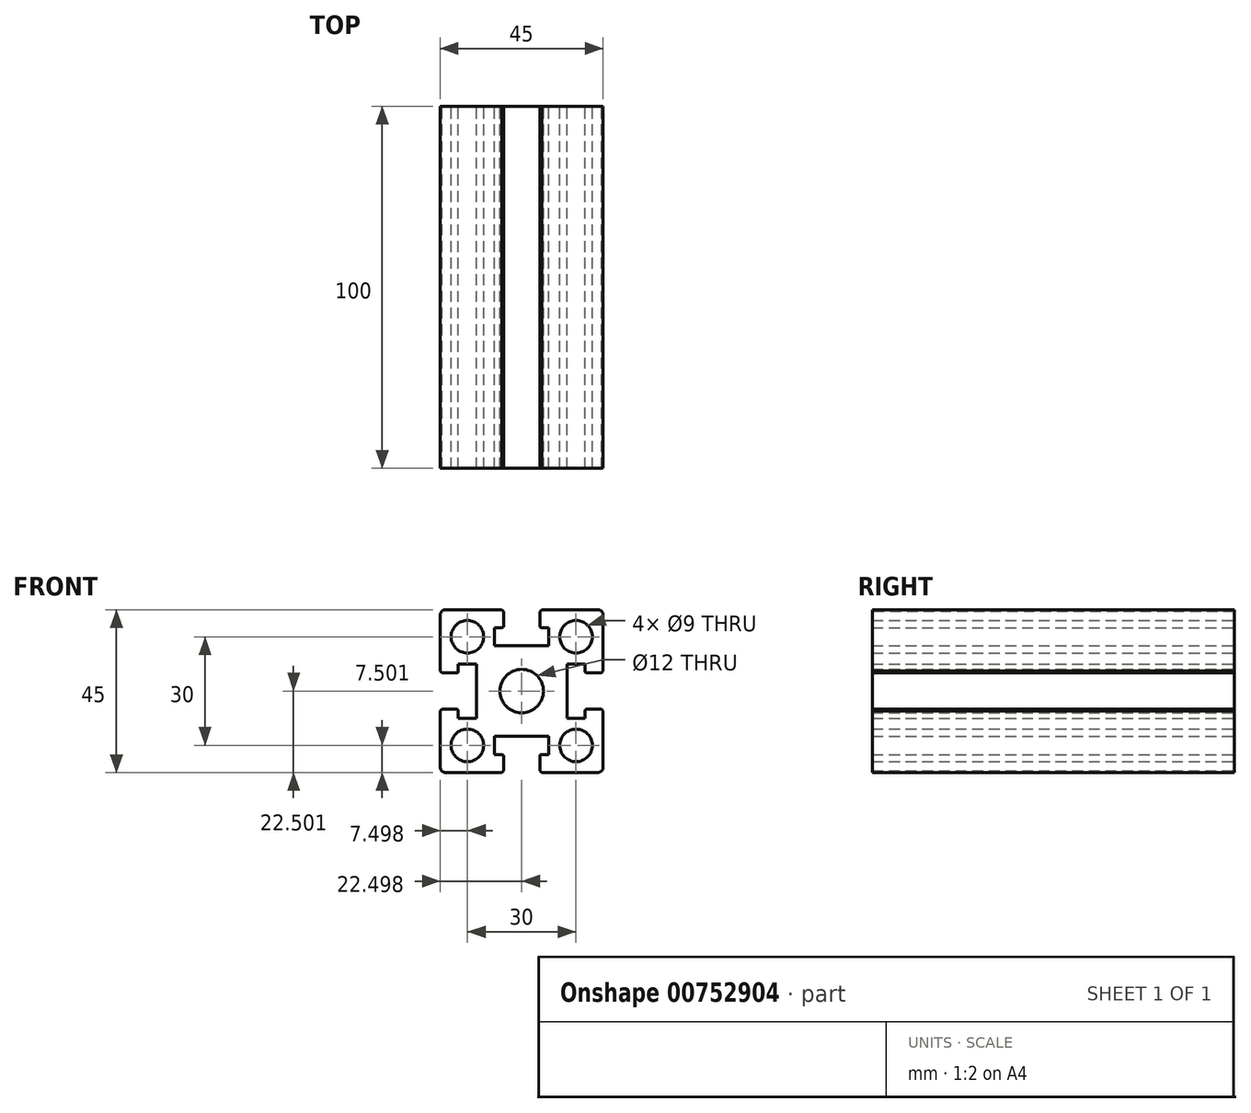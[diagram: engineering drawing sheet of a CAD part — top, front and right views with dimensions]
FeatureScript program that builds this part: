
annotation { "Feature Type Name" : "Feature", "Feature Type Description" : "" }
export const myFeature = defineFeature(function(context is Context, id is Id, definition is map)
    precondition{}
    {
        {
            var Q0;
            Q0=qCreatedBy(makeId("Front.planeOp"),FACE);
            var sketch = newSketch(context, id + "F0", { "sketchPlane" : qUnion([Q0])});
            skLineSegment(sketch, "E0.left", {"start": v(21.62, -21.03) * mm, "end": v(21.62, -3.53) * mm});
            skLineSegment(sketch, "E0.right", {"start": v(-23.38, -21.03) * mm, "end": v(-23.38, -3.53) * mm});
            skPoint(sketch, "E0.middle", {"position": v(-0.88, 1.47) * mm});
            skCircle(sketch, "E1", {"center": v(-0.88, 1.47) * mm, "radius": 6 * mm});
            skLineSegment(sketch, "E2.bottom", {"start": v(-23.38, 6.47) * mm, "end": v(-18.38, 6.47) * mm});
            skLineSegment(sketch, "E2.top", {"start": v(-23.38, -3.53) * mm, "end": v(-18.38, -3.53) * mm});
            skLineSegment(sketch, "E3", {"start": v(-18.38, 6.47) * mm, "end": v(-18.38, 8.97) * mm});
            skLineSegment(sketch, "E4", {"start": v(-18.38, 8.97) * mm, "end": v(-13.38, 8.97) * mm});
            skLineSegment(sketch, "E5", {"start": v(-13.38, 8.97) * mm, "end": v(-13.38, -6.03) * mm});
            skLineSegment(sketch, "E6", {"start": v(-18.38, -3.53) * mm, "end": v(-18.38, -6.03) * mm});
            skLineSegment(sketch, "E7", {"start": v(-18.38, -6.03) * mm, "end": v(-13.38, -6.03) * mm});
            skLineSegment(sketch, "E8.trimOffspring", {"start": v(-23.38, 6.47) * mm, "end": v(-23.38, 23.97) * mm});
            skLineSegment(sketch, "E9.MirrorCS", {"start": v(21.62, -3.53) * mm, "end": v(16.62, -3.53) * mm});
            skLineSegment(sketch, "E10.MirrorCS", {"start": v(16.62, -6.03) * mm, "end": v(11.62, -6.03) * mm});
            skLineSegment(sketch, "E11.MirrorCS", {"start": v(11.62, 8.97) * mm, "end": v(11.62, -6.03) * mm});
            skLineSegment(sketch, "E12.MirrorCS", {"start": v(16.62, 8.97) * mm, "end": v(11.62, 8.97) * mm});
            skLineSegment(sketch, "E13.MirrorCS", {"start": v(21.62, 6.47) * mm, "end": v(16.62, 6.47) * mm});
            skLineSegment(sketch, "E14", {"start": v(16.62, 8.97) * mm, "end": v(16.62, 6.47) * mm});
            skLineSegment(sketch, "E15", {"start": v(16.62, -3.53) * mm, "end": v(16.62, -6.03) * mm});
            skLineSegment(sketch, "E16.trimOffspring", {"start": v(21.62, 6.47) * mm, "end": v(21.62, 23.97) * mm});
            skPoint(sketch, "E17", {"position": v(14.12, -13.53) * mm});
            skPoint(sketch, "E18", {"position": v(14.12, 16.47) * mm});
            skPoint(sketch, "E19", {"position": v(-15.88, 16.47) * mm});
            skPoint(sketch, "E20", {"position": v(-15.88, -13.53) * mm});
            skCircle(sketch, "E21", {"center": v(14.12, -13.53) * mm, "radius": 4.5 * mm});
            skCircle(sketch, "E22", {"center": v(-15.88, -13.53) * mm, "radius": 4.5 * mm});
            skCircle(sketch, "E23", {"center": v(-15.88, 16.47) * mm, "radius": 4.5 * mm});
            skCircle(sketch, "E24", {"center": v(14.12, 16.47) * mm, "radius": 4.5 * mm});
            skLineSegment(sketch, "E25", {"start": v(-23.38, 23.97) * mm, "end": v(-5.88, 23.97) * mm});
            skLineSegment(sketch, "E26", {"start": v(-23.38, -21.03) * mm, "end": v(-5.88, -21.03) * mm});
            skLineSegment(sketch, "E27.left", {"start": v(-5.88, 23.97) * mm, "end": v(-5.88, 18.97) * mm});
            skLineSegment(sketch, "E27.right", {"start": v(4.12, 23.97) * mm, "end": v(4.12, 18.97) * mm});
            skLineSegment(sketch, "E28.bottom", {"start": v(-8.38, 18.97) * mm, "end": v(-5.88, 18.97) * mm});
            skLineSegment(sketch, "E28.top", {"start": v(-8.38, 13.97) * mm, "end": v(6.62, 13.97) * mm});
            skLineSegment(sketch, "E28.left", {"start": v(-8.38, 18.97) * mm, "end": v(-8.38, 13.97) * mm});
            skLineSegment(sketch, "E28.right", {"start": v(6.62, 18.97) * mm, "end": v(6.62, 13.97) * mm});
            skLineSegment(sketch, "E29.trimOffspring", {"start": v(4.12, 23.97) * mm, "end": v(21.62, 23.97) * mm});
            skLineSegment(sketch, "E30.trimOffspring", {"start": v(4.12, 18.97) * mm, "end": v(6.62, 18.97) * mm});
            skLineSegment(sketch, "E31.left", {"start": v(-5.88, -21.03) * mm, "end": v(-5.88, -16.03) * mm});
            skLineSegment(sketch, "E31.right", {"start": v(4.12, -21.03) * mm, "end": v(4.12, -16.03) * mm});
            skLineSegment(sketch, "E32.bottom", {"start": v(-8.38, -11.03) * mm, "end": v(6.62, -11.03) * mm});
            skLineSegment(sketch, "E32.top", {"start": v(-8.38, -16.03) * mm, "end": v(-5.88, -16.03) * mm});
            skLineSegment(sketch, "E32.left", {"start": v(-8.38, -11.03) * mm, "end": v(-8.38, -16.03) * mm});
            skLineSegment(sketch, "E32.right", {"start": v(6.62, -11.03) * mm, "end": v(6.62, -16.03) * mm});
            skLineSegment(sketch, "E33.bottom", {"start": v(6.62, -11.03) * mm, "end": v(6.62, -11.03) * mm});
            skLineSegment(sketch, "E33.top", {"start": v(6.62, -16.03) * mm, "end": v(6.62, -16.03) * mm});
            skLineSegment(sketch, "E34.trimOffspring", {"start": v(4.12, -16.03) * mm, "end": v(6.62, -16.03) * mm});
            skLineSegment(sketch, "E35.trimOffspring", {"start": v(4.12, -21.03) * mm, "end": v(21.62, -21.03) * mm});
            skSolve(sketch);
        }
        {
            var Q0;
            Q0=makeQuery(id+"F0.imprint","IMPRINT",FACE,{"disambiguationData":[TD([[makeQuery(id+"F0.imprint","IMPRINT",EDGE,{"derivedFrom":sQuery(id+"F0.wireOp",EDGE,"E0.left")}),1.0]])]});
            extrude(context, id + "F1", {"entities" : qUnion([Q0]), "depth" : 100 * mm, "offsetDistance" : 25 * mm});
        }
        {
            var Q0;
            Q0=makeQuery(id+"F1.opExtrude","SWEPT_EDGE",EDGE,{"disambiguationData":[OSD([sQuery(id+"F0.wireOp",EDGE,"E16.trimOffspring"),sQuery(id+"F0.wireOp",EDGE,"E29.trimOffspring")])]});
            var Q1;
            Q1=makeQuery(id+"F1.opExtrude","SWEPT_EDGE",EDGE,{"disambiguationData":[OSD([sQuery(id+"F0.wireOp",EDGE,"E0.left"),sQuery(id+"F0.wireOp",EDGE,"E35.trimOffspring")])]});
            var Q2;
            Q2=makeQuery(id+"F1.opExtrude","SWEPT_EDGE",EDGE,{"disambiguationData":[OSD([sQuery(id+"F0.wireOp",EDGE,"E8.trimOffspring"),sQuery(id+"F0.wireOp",EDGE,"E25")])]});
            var Q3;
            Q3=makeQuery(id+"F1.opExtrude","SWEPT_EDGE",EDGE,{"disambiguationData":[OSD([sQuery(id+"F0.wireOp",EDGE,"E0.right"),sQuery(id+"F0.wireOp",EDGE,"E26")])]});
            fillet(context, id + "F2", {"entities" : qUnion([Q0, Q1, Q2, Q3]), "radius" : 1.5 * mm, "tangentPropagation" : true, "allowEdgeOverflow" : false});
        }
        {
            var Q0;
            Q0=makeQuery(id+"F1.opExtrude","SWEPT_EDGE",EDGE,{"disambiguationData":[OSD([sQuery(id+"F0.wireOp",EDGE,"E2.bottom"),sQuery(id+"F0.wireOp",EDGE,"E3")])]});
            var Q1;
            Q1=makeQuery(id+"F1.opExtrude","SWEPT_EDGE",EDGE,{"disambiguationData":[OSD([sQuery(id+"F0.wireOp",EDGE,"E27.left"),sQuery(id+"F0.wireOp",EDGE,"E28.bottom")])]});
            var Q2;
            Q2=makeQuery(id+"F1.opExtrude","SWEPT_EDGE",EDGE,{"disambiguationData":[OSD([sQuery(id+"F0.wireOp",EDGE,"E27.right"),sQuery(id+"F0.wireOp",EDGE,"E30.trimOffspring")])]});
            var Q3;
            Q3=makeQuery(id+"F1.opExtrude","SWEPT_EDGE",EDGE,{"disambiguationData":[OSD([sQuery(id+"F0.wireOp",EDGE,"E13.MirrorCS"),sQuery(id+"F0.wireOp",EDGE,"E14")])]});
            var Q4;
            Q4=makeQuery(id+"F1.opExtrude","SWEPT_EDGE",EDGE,{"disambiguationData":[OSD([sQuery(id+"F0.wireOp",EDGE,"E31.right"),sQuery(id+"F0.wireOp",EDGE,"E34.trimOffspring")])]});
            var Q5;
            Q5=makeQuery(id+"F1.opExtrude","SWEPT_EDGE",EDGE,{"disambiguationData":[OSD([sQuery(id+"F0.wireOp",EDGE,"E9.MirrorCS"),sQuery(id+"F0.wireOp",EDGE,"E15")])]});
            var Q6;
            Q6=makeQuery(id+"F1.opExtrude","SWEPT_EDGE",EDGE,{"disambiguationData":[OSD([sQuery(id+"F0.wireOp",EDGE,"E31.left"),sQuery(id+"F0.wireOp",EDGE,"E32.top")])]});
            var Q7;
            Q7=makeQuery(id+"F1.opExtrude","SWEPT_EDGE",EDGE,{"disambiguationData":[OSD([sQuery(id+"F0.wireOp",EDGE,"E2.top"),sQuery(id+"F0.wireOp",EDGE,"E6")])]});
            fillet(context, id + "F3", {"entities" : qUnion([Q0, Q1, Q2, Q3, Q4, Q5, Q6, Q7]), "radius" : .5 * mm, "tangentPropagation" : true, "allowEdgeOverflow" : false});
        }
        {
            var Q0;
            Q0=makeQuery(id+"F1.opExtrude","SWEPT_EDGE",EDGE,{"disambiguationData":[OSD([sQuery(id+"F0.wireOp",EDGE,"E25"),sQuery(id+"F0.wireOp",EDGE,"E27.left")])]});
            var Q1;
            Q1=makeQuery(id+"F1.opExtrude","SWEPT_EDGE",EDGE,{"disambiguationData":[OSD([sQuery(id+"F0.wireOp",EDGE,"E27.right"),sQuery(id+"F0.wireOp",EDGE,"E29.trimOffspring")])]});
            var Q2;
            Q2=makeQuery(id+"F1.opExtrude","SWEPT_EDGE",EDGE,{"disambiguationData":[OSD([sQuery(id+"F0.wireOp",EDGE,"E13.MirrorCS"),sQuery(id+"F0.wireOp",EDGE,"E16.trimOffspring")])]});
            var Q3;
            Q3=makeQuery(id+"F1.opExtrude","SWEPT_EDGE",EDGE,{"disambiguationData":[OSD([sQuery(id+"F0.wireOp",EDGE,"E0.left"),sQuery(id+"F0.wireOp",EDGE,"E9.MirrorCS")])]});
            var Q4;
            Q4=makeQuery(id+"F1.opExtrude","SWEPT_EDGE",EDGE,{"disambiguationData":[OSD([sQuery(id+"F0.wireOp",EDGE,"E26"),sQuery(id+"F0.wireOp",EDGE,"E31.left")])]});
            var Q5;
            Q5=makeQuery(id+"F1.opExtrude","SWEPT_EDGE",EDGE,{"disambiguationData":[OSD([sQuery(id+"F0.wireOp",EDGE,"E0.right"),sQuery(id+"F0.wireOp",EDGE,"E2.top")])]});
            var Q6;
            Q6=makeQuery(id+"F1.opExtrude","SWEPT_EDGE",EDGE,{"disambiguationData":[OSD([sQuery(id+"F0.wireOp",EDGE,"E2.bottom"),sQuery(id+"F0.wireOp",EDGE,"E8.trimOffspring")])]});
            var Q7;
            Q7=makeQuery(id+"F1.opExtrude","SWEPT_EDGE",EDGE,{"disambiguationData":[OSD([sQuery(id+"F0.wireOp",EDGE,"E31.right"),sQuery(id+"F0.wireOp",EDGE,"E35.trimOffspring")])]});
            chamfer(context, id + "F4", {"entities" : qUnion([Q0, Q1, Q2, Q3, Q4, Q5, Q6, Q7]), "width" : .5 * mm, "tangentPropagation" : true});
        }
    });
